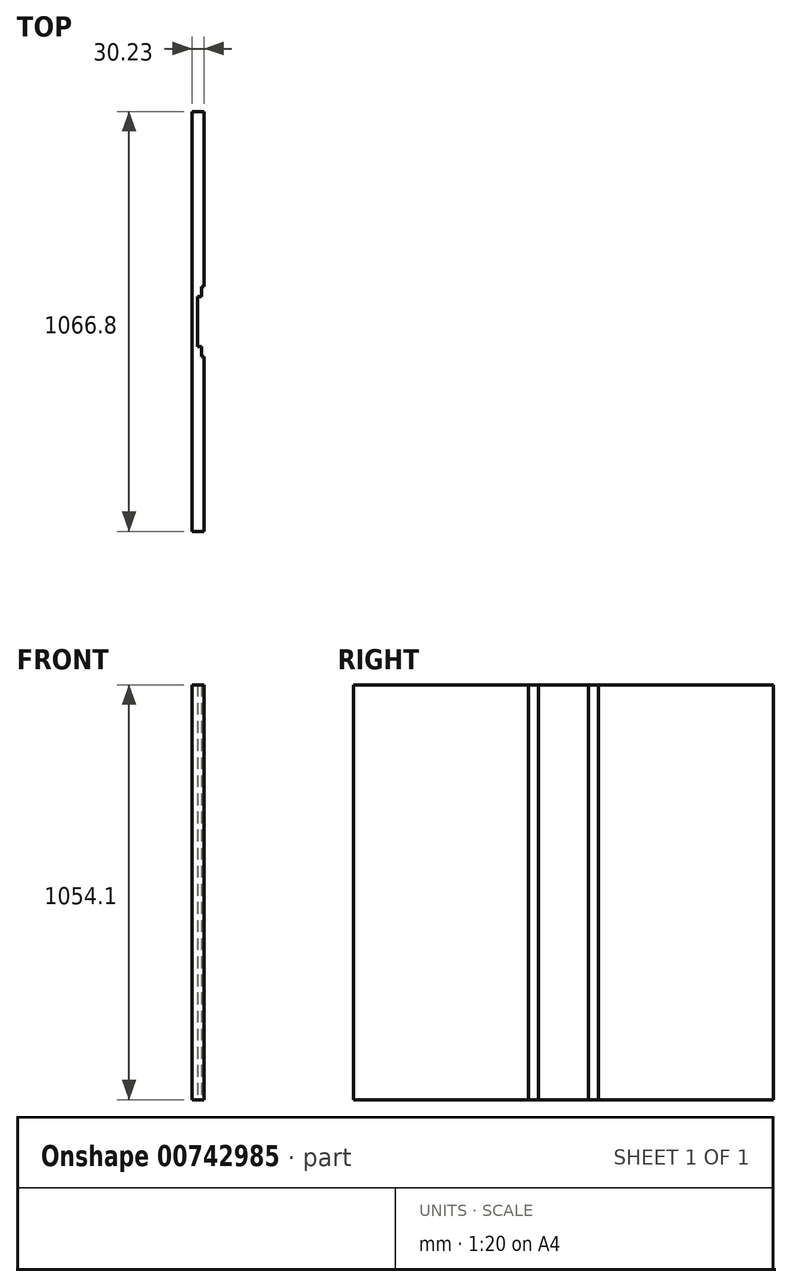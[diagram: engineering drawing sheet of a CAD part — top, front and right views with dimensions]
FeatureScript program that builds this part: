
annotation { "Feature Type Name" : "Feature", "Feature Type Description" : "" }
export const myFeature = defineFeature(function(context is Context, id is Id, definition is map)
    precondition{}
    {
        {
            var Q0;
            Q0=qCreatedBy(makeId("Right.planeOp"),FACE);
            var sketch = newSketch(context, id + "F0", { "sketchPlane" : qUnion([Q0])});
            skLineSegment(sketch, "E0.bottom", {"start": v(533.4, 527.05) * mm, "end": v(-533.4, 527.05) * mm});
            skLineSegment(sketch, "E0.top", {"start": v(533.4, -527.05) * mm, "end": v(-533.4, -527.05) * mm});
            skLineSegment(sketch, "E0.left", {"start": v(533.4, 527.05) * mm, "end": v(533.4, -527.05) * mm});
            skLineSegment(sketch, "E0.right", {"start": v(-533.4, 527.05) * mm, "end": v(-533.4, -527.05) * mm});
            skPoint(sketch, "E0.middle", {"position": v(0, 0) * mm});
            skSolve(sketch);
        }
        {
            var Q0;
            Q0=makeQuery(id+"F0.imprint","IMPRINT",FACE,{"disambiguationData":[TD([[makeQuery(id+"F0.imprint","IMPRINT",EDGE,{"derivedFrom":sQuery(id+"F0.wireOp",EDGE,"E0.bottom")}),1.0]])]});
            extrude(context, id + "F1", {"entities" : qUnion([Q0]), "depth" : 30.23 * mm, "offsetDistance" : 25.4 * mm});
        }
        {
            var Q0;
            Q0=makeQuery(id+"F1.opExtrude","CAP_FACE",FACE,{"disambiguationData":[OSD([sQuery(id+"F0.wireOp",EDGE,"E0.bottom"),sQuery(id+"F0.wireOp",EDGE,"E0.top"),sQuery(id+"F0.wireOp",EDGE,"E0.left"),sQuery(id+"F0.wireOp",EDGE,"E0.right")])],"isStart":false});
            var sketch = newSketch(context, id + "F2", { "sketchPlane" : qUnion([Q0])});
            skLineSegment(sketch, "E1.bottom", {"start": v(88.9, 527.05) * mm, "end": v(-88.9, 527.05) * mm});
            skLineSegment(sketch, "E1.top", {"start": v(88.9, -527.05) * mm, "end": v(-88.9, -527.05) * mm});
            skLineSegment(sketch, "E1.left", {"start": v(88.9, 527.05) * mm, "end": v(88.9, -527.05) * mm});
            skLineSegment(sketch, "E1.right", {"start": v(-88.9, 527.05) * mm, "end": v(-88.9, -527.05) * mm});
            skPoint(sketch, "E1.middle", {"position": v(0, 0) * mm});
            skSolve(sketch);
        }
        {
            var Q0;
            Q0=makeQuery(id+"F2.imprint","IMPRINT",FACE,{"disambiguationData":[TD([[makeQuery(id+"F2.imprint","IMPRINT",EDGE,{"derivedFrom":sQuery(id+"F2.wireOp",EDGE,"E1.bottom")}),1.0]])]});
            extrude(context, id + "F3", {"entities" : qUnion([Q0]), "operationType" : NewBodyOperationType.REMOVE, "oppositeDirection" : true, "depth" : 6.35 * mm, "offsetDistance" : 25.4 * mm});
        }
        {
            var Q0;
            Q0=makeQuery(id+"F3.boolean.opBoolean","COPY",FACE,{"derivedFrom":makeQuery(id+"F3.opExtrude","CAP_FACE",FACE,{"disambiguationData":[OSD([sQuery(id+"F2.wireOp",EDGE,"E1.bottom"),sQuery(id+"F2.wireOp",EDGE,"E1.top"),sQuery(id+"F2.wireOp",EDGE,"E1.left"),sQuery(id+"F2.wireOp",EDGE,"E1.right")])],"isStart":false})});
            var sketch = newSketch(context, id + "F4", { "sketchPlane" : qUnion([Q0])});
            skLineSegment(sketch, "E2.bottom", {"start": v(63.5, 527.05) * mm, "end": v(-63.5, 527.05) * mm});
            skLineSegment(sketch, "E2.top", {"start": v(63.5, -527.05) * mm, "end": v(-63.5, -527.05) * mm});
            skLineSegment(sketch, "E2.left", {"start": v(63.5, 527.05) * mm, "end": v(63.5, -527.05) * mm});
            skLineSegment(sketch, "E2.right", {"start": v(-63.5, 527.05) * mm, "end": v(-63.5, -527.05) * mm});
            skPoint(sketch, "E2.middle", {"position": v(0, 0) * mm});
            skSolve(sketch);
        }
        {
            var Q0;
            Q0=makeQuery(id+"F4.imprint","IMPRINT",FACE,{"disambiguationData":[TD([[makeQuery(id+"F4.imprint","IMPRINT",EDGE,{"derivedFrom":sQuery(id+"F4.wireOp",EDGE,"E2.bottom")}),1.0]])]});
            extrude(context, id + "F5", {"entities" : qUnion([Q0]), "operationType" : NewBodyOperationType.REMOVE, "oppositeDirection" : true, "depth" : 9.52 * mm, "offsetDistance" : 25.4 * mm});
        }
    });
